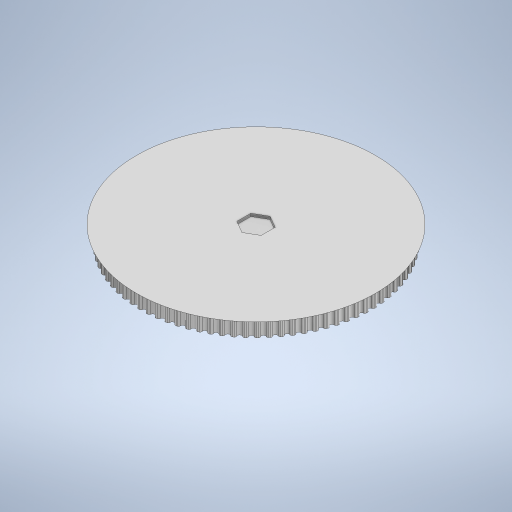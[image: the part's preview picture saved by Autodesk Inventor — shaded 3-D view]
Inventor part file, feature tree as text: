
AUTODESK INVENTOR PART (.ipt)
format: ipt  version: 2024 (Build 280153000, 153)  size: 1,314,304 bytes
history: native  units: mm
features: sketch x7, extrude x6, pattern_circular x1, fillet x1, chamfer x1, projected_geometry x1
ambient origin geometry x8: Origin, YZ Plane, XZ Plane, XY Plane, X Axis, Y Axis, Z Axis, Center Point
bodies: Solid1 (feature_tree)
feature tree (17):
  extrude  "Extrusion1"  Depth=25.0mm TaperAngle=0.0deg
  extrude  "Extrusion2"  Depth=2.0mm TaperAngle=0.0deg
  extrude  "Extrusion3"  Depth=164.0mm
  extrude  "Extrusion4"  Depth=10.0mm TaperAngle=360.0deg
  pattern_circular  "Circular Pattern1"  [2 undecoded]
  extrude  "Extrusion5"  Depth=1.15mm
  extrude  "Extrusion6"  Depth=4.0mm TaperAngle=45.0deg
  fillet  "Fillet1"  [1 undecoded]
  sketch  "Sketch8"  dims[d18=3.0mm d19=2.0mm d20=0.0mm d21=1.15mm d23=4.0mm d24=2.0mm d25=45.0deg]
  chamfer  "Chamfer1"  [1 undecoded]
  sketch  "Sketch1"  dims[d0=20.0mm d1=25.0mm d2=0.0mm]
  sketch  "Sketch2"  dims[d3=40.0mm d4=2.0mm d5=0.0mm]
  sketch  "Sketch3"  dims[d6=12.0mm d7=0.0mm d8=164.0mm]
  sketch  "Sketch4"  dims[d9=10.0mm d10=0.0mm d11=850.0mm d12=360.0deg]
  sketch  "Sketch6"  dims[d15=2.0mm d16=0.0mm]
  sketch  "Sketch7"  dims[d17=10.0mm]
  projected_geometry  "Projected Loop1"
note: 4 required parameter values undecoded (feature->parameter linkage not recoverable at this tier; creation-order binding heuristic only, values carry confidence <= 0.55)
